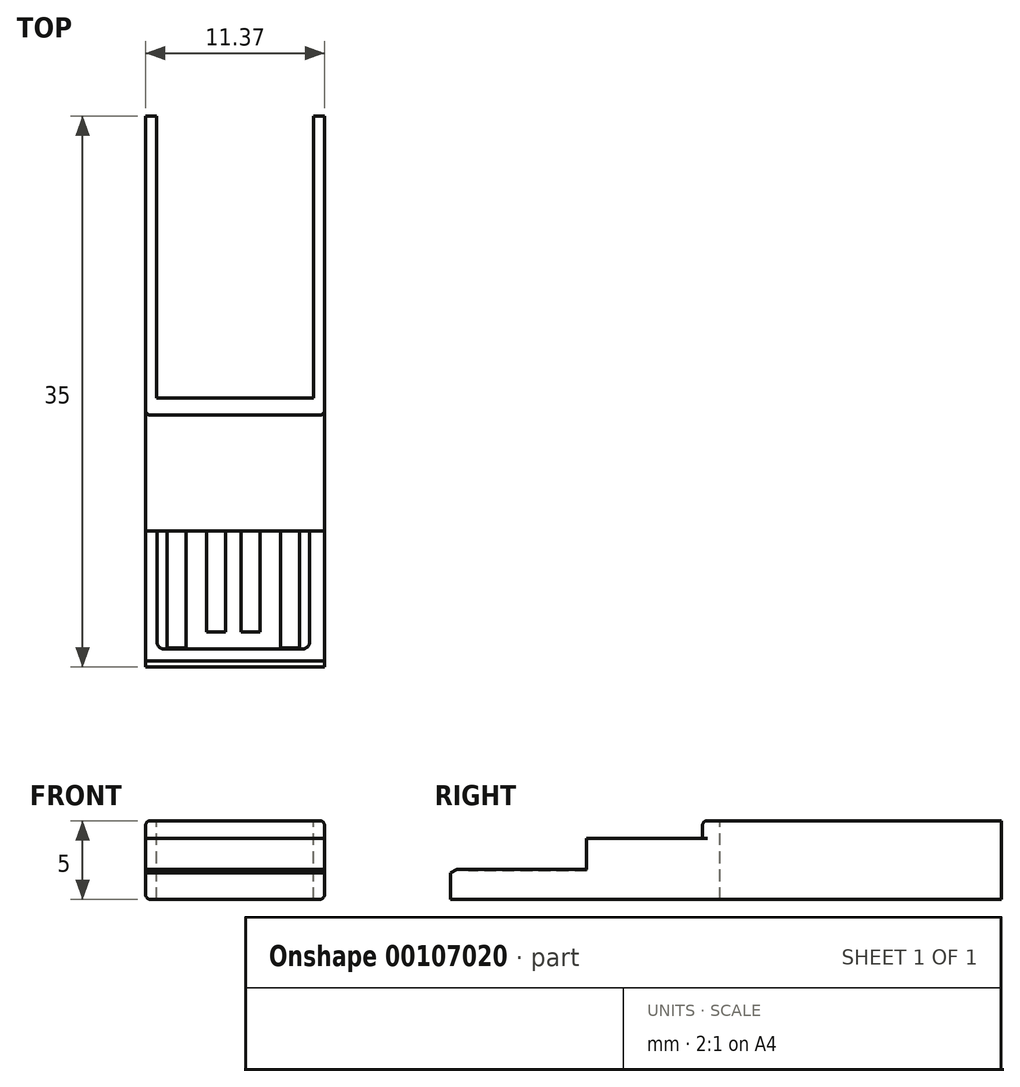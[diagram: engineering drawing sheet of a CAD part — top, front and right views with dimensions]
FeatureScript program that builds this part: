
annotation { "Feature Type Name" : "Feature", "Feature Type Description" : "" }
export const myFeature = defineFeature(function(context is Context, id is Id, definition is map)
    precondition{}
    {
        {
            var Q0;
            Q0=qCreatedBy(makeId("Front.planeOp"),FACE);
            var sketch = newSketch(context, id + "F0", { "sketchPlane" : qUnion([Q0])});
            skLineSegment(sketch, "E0.bottom", {"start": v(0, 0) * mm, "end": v(11.37, 0) * mm});
            skLineSegment(sketch, "E0.top", {"start": v(0, 1.92) * mm, "end": v(11.37, 1.92) * mm});
            skLineSegment(sketch, "E0.left", {"start": v(0, 0) * mm, "end": v(0, 1.92) * mm});
            skLineSegment(sketch, "E0.right", {"start": v(11.37, 0) * mm, "end": v(11.37, 1.92) * mm});
            skSolve(sketch);
        }
        {
            var Q0;
            Q0=qSketchRegion(id+"F0",true);
            extrude(context, id + "F1", {"entities" : qUnion([Q0]), "depth" : 35 * mm});
        }
        {
            var Q0;
            Q0=makeQuery(id+"F1.opExtrude","CAP_EDGE",EDGE,{"disambiguationData":[OSD([sQuery(id+"F0.wireOp",EDGE,"E0.top")])],"isStart":false});
            chamfer(context, id + "F2", {"entities" : qUnion([Q0]), "chamferType" : ChamferType.OFFSET_ANGLE, "width" : .4 * mm, "oppositeDirection" : false, "angle" : 30 * degree, "tangentPropagation" : true});
        }
        {
            var Q0;
            Q0=makeQuery(id+"F1.opExtrude","CAP_FACE",FACE,{"disambiguationData":[OSD([sQuery(id+"F0.wireOp",EDGE,"E0.bottom"),sQuery(id+"F0.wireOp",EDGE,"E0.top"),sQuery(id+"F0.wireOp",EDGE,"E0.left"),sQuery(id+"F0.wireOp",EDGE,"E0.right"),sQuery(id+"F0.wireOp",EDGE,"56C0QhvD-F77E-lm7p-6VUG-UG7dpPcv46jt.top"),sQuery(id+"F0.wireOp",EDGE,"56C0QhvD-F77E-lm7p-6VUG-UG7dpPcv46jt.left"),sQuery(id+"F0.wireOp",EDGE,"56C0QhvD-F77E-lm7p-6VUG-UG7dpPcv46jt.right"),sQuery(id+"F0.wireOp",EDGE,"f6b8b6c7-bbb4-4efb-80b2-3a6712df3d87.trimOffspring")])],"isStart":true});
            var sketch = newSketch(context, id + "F3", { "sketchPlane" : qUnion([Q0])});
            skLineSegment(sketch, "E1.bottom", {"start": v(0, 1.92) * mm, "end": v(-11.37, 1.92) * mm});
            skLineSegment(sketch, "E1.top", {"start": v(0, 3.87) * mm, "end": v(-11.37, 3.87) * mm});
            skLineSegment(sketch, "E1.left", {"start": v(0, 1.92) * mm, "end": v(0, 3.87) * mm});
            skLineSegment(sketch, "E1.right", {"start": v(-11.37, 1.92) * mm, "end": v(-11.37, 3.87) * mm});
            skSolve(sketch);
        }
        {
            var Q0;
            Q0=qSketchRegion(id+"F3",true);
            extrude(context, id + "F4", {"entities" : qUnion([Q0]), "operationType" : NewBodyOperationType.ADD, "oppositeDirection" : true, "depth" : 26.35 * mm});
        }
        {
            var Q0;
            {var subQ0=sQuery(id+"F0.wireOp",EDGE,"E0.top");Q0=makeQuery(id+"F5PljUPMjGb4KAi_1.boolean.opBoolean","SPLIT",FACE,{"disambiguationData":[TD([makeQuery(id+"F2.opChamfer","BLEND_FACE",FACE,{"disambiguationData":[OSD([subQ0])]})])],"derivedFrom":makeQuery(id+"F1.opExtrude","SWEPT_FACE",FACE,{"disambiguationData":[OSD([subQ0])]})});}
            var sketch = newSketch(context, id + "F5", { "sketchPlane" : qUnion([Q0])});
            skLineSegment(sketch, "E2", {"start": v(5.57, -14.35) * mm, "end": v(5.57, -24.55) * mm, "construction": true});
            skLineSegment(sketch, "E3.bottom", {"start": v(0.72, -26.36) * mm, "end": v(10.42, -26.36) * mm});
            skLineSegment(sketch, "E3.top", {"start": v(1.22, -33.86) * mm, "end": v(9.92, -33.86) * mm});
            skLineSegment(sketch, "E3.left", {"start": v(0.72, -26.36) * mm, "end": v(0.72, -33.36) * mm});
            skLineSegment(sketch, "E3.right", {"start": v(10.42, -26.36) * mm, "end": v(10.42, -33.36) * mm});
            skPoint(sketch, "E3.middle", {"position": v(5.57, -30.1) * mm});
            skPoint(sketch, "E4.visualSharp", {"position": v(0.72, -33.86) * mm});
            skArc(sketch, "E4.filletArc", {"start": v(0.72, -33.36) * mm, "mid": v(0.87, -33.7) * mm, "end": v(1.22, -33.86) * mm});
            skPoint(sketch, "E5.visualSharp", {"position": v(10.42, -33.86) * mm});
            skArc(sketch, "E5.filletArc", {"start": v(9.92, -33.86) * mm, "mid": v(10.28, -33.7) * mm, "end": v(10.42, -33.36) * mm});
            skSolve(sketch);
        }
        {
            var Q0;
            Q0=qSketchRegion(id+"F5",true);
            extrude(context, id + "F6", {"entities" : qUnion([Q0]), "operationType" : NewBodyOperationType.REMOVE, "oppositeDirection" : true, "depth" : .1 * mm});
        }
        {
            var Q0;
            Q0=makeQuery(id+"F6.boolean.opBoolean","COPY",FACE,{"derivedFrom":makeQuery(id+"F6.opExtrude","CAP_FACE",FACE,{"disambiguationData":[OSD([sQuery(id+"F5.wireOp",EDGE,"E3.bottom"),sQuery(id+"F5.wireOp",EDGE,"E3.top"),sQuery(id+"F5.wireOp",EDGE,"E3.left"),sQuery(id+"F5.wireOp",EDGE,"E3.right"),sQuery(id+"F5.wireOp",EDGE,"E4.filletArc"),sQuery(id+"F5.wireOp",EDGE,"E5.filletArc")])],"isStart":false})});
            var sketch = newSketch(context, id + "F7", { "sketchPlane" : qUnion([Q0])});
            skLineSegment(sketch, "E6.bottom", {"start": v(5.57, -26.36) * mm, "end": v(5.57, -26.36) * mm});
            skLineSegment(sketch, "E6.top", {"start": v(5.57, -33.86) * mm, "end": v(5.57, -33.86) * mm});
            skLineSegment(sketch, "E6.left", {"start": v(5.57, -26.36) * mm, "end": v(5.57, -33.86) * mm, "construction": true});
            skLineSegment(sketch, "E6.right", {"start": v(5.57, -26.36) * mm, "end": v(5.57, -33.86) * mm, "construction": true});
            skLineSegment(sketch, "E7.bottom", {"start": v(3.87, -26.36) * mm, "end": v(5.07, -26.36) * mm});
            skLineSegment(sketch, "E7.top", {"start": v(3.87, -32.77) * mm, "end": v(5.07, -32.77) * mm});
            skLineSegment(sketch, "E7.left", {"start": v(3.87, -26.36) * mm, "end": v(3.87, -32.77) * mm});
            skLineSegment(sketch, "E7.right", {"start": v(5.07, -26.36) * mm, "end": v(5.07, -32.77) * mm});
            skLineSegment(sketch, "E8.bottom", {"start": v(1.37, -26.36) * mm, "end": v(2.57, -26.36) * mm});
            skLineSegment(sketch, "E8.top", {"start": v(1.37, -33.77) * mm, "end": v(2.57, -33.77) * mm});
            skLineSegment(sketch, "E8.left", {"start": v(1.37, -26.36) * mm, "end": v(1.37, -33.77) * mm});
            skLineSegment(sketch, "E8.right", {"start": v(2.57, -26.36) * mm, "end": v(2.57, -33.77) * mm});
            skLineSegment(sketch, "E9.MirrorCS", {"start": v(7.27, -26.36) * mm, "end": v(6.07, -26.36) * mm});
            skLineSegment(sketch, "E10.MirrorCS", {"start": v(7.27, -32.77) * mm, "end": v(6.07, -32.77) * mm});
            skLineSegment(sketch, "E11.MirrorCS", {"start": v(7.27, -26.36) * mm, "end": v(7.27, -32.77) * mm});
            skLineSegment(sketch, "E12.MirrorCS", {"start": v(6.07, -26.36) * mm, "end": v(6.07, -32.77) * mm});
            skLineSegment(sketch, "E13.MirrorCS", {"start": v(9.77, -26.36) * mm, "end": v(8.57, -26.36) * mm});
            skLineSegment(sketch, "E14.MirrorCS", {"start": v(9.77, -33.77) * mm, "end": v(8.57, -33.77) * mm});
            skLineSegment(sketch, "E15.MirrorCS", {"start": v(9.77, -26.36) * mm, "end": v(9.77, -33.77) * mm});
            skLineSegment(sketch, "E16.MirrorCS", {"start": v(8.57, -26.36) * mm, "end": v(8.57, -33.77) * mm});
            skSolve(sketch);
        }
        {
            var Q0;
            Q0=qSketchRegion(id+"F7",true);
            var Q1;
            {var subQ0=sQuery(id+"F0.wireOp",EDGE,"E0.top");Q1=makeQuery(id+"F5PljUPMjGb4KAi_1.boolean.opBoolean","SPLIT",FACE,{"disambiguationData":[TD([makeQuery(id+"F2.opChamfer","BLEND_FACE",FACE,{"disambiguationData":[OSD([subQ0])]})])],"derivedFrom":makeQuery(id+"F1.opExtrude","SWEPT_FACE",FACE,{"disambiguationData":[OSD([subQ0])]})});}
            extrude(context, id + "F8", {"entities" : qUnion([Q0]), "operationType" : NewBodyOperationType.ADD, "endBound" : BoundingType.UP_TO_SURFACE, "endBoundEntityFace" : qUnion([Q1]), "depth" : 25 * mm});
        }
        {
            var Q0;
            {var subQ0=sQuery(id+"F3.wireOp",EDGE,"E1.top");Q0=makeQuery(id+"FO6QDnWpxEzhnGm_1.boolean.opBoolean","MERGE",FACE,{"derivedFrom":[makeQuery(id+"F4.opExtrude","SWEPT_FACE",FACE,{"disambiguationData":[OSD([subQ0])]}),makeQuery(id+"F5PljUPMjGb4KAi_1.opExtrude","CAP_FACE",FACE,{"disambiguationData":[OSD([subQ0])],"isStart":false}),makeQuery(id+"FO6QDnWpxEzhnGm_1.opExtrude","SWEPT_FACE",FACE,{"disambiguationData":[OSD([sQuery(id+"F6S5VhLR9gniqHa_1.wireOp",EDGE,"7c9bdd74-e41c-4fc5-a593-b1e6411b71d9.0")])]})]});}
            var sketch = newSketch(context, id + "F9", { "sketchPlane" : qUnion([Q0])});
            skLineSegment(sketch, "E17.bottom", {"start": v(11.37, 0) * mm, "end": v(0, 0) * mm});
            skLineSegment(sketch, "E17.top", {"start": v(11.37, -19) * mm, "end": v(0, -19) * mm});
            skLineSegment(sketch, "E17.left", {"start": v(11.37, 0) * mm, "end": v(11.37, -19) * mm});
            skLineSegment(sketch, "E17.right", {"start": v(0, 0) * mm, "end": v(0, -19) * mm});
            skSolve(sketch);
        }
        {
            var Q0;
            Q0 = qSketchRegion(id + "F9", true);
            extrude(context, id + "F10", {"entities" : qUnion([Q0]), "operationType" : NewBodyOperationType.ADD, "depth" : 1.13 * mm});
        }
        {
            var Q0;
            Q0=makeQuery(id+"F10.opExtrude","CAP_FACE",FACE,{"disambiguationData":[OSD([sQuery(id+"F9.wireOp",EDGE,"E17.bottom"),sQuery(id+"F9.wireOp",EDGE,"E17.top"),sQuery(id+"F9.wireOp",EDGE,"E17.left"),sQuery(id+"F9.wireOp",EDGE,"E17.right")])],"isStart":false});
            var sketch = newSketch(context, id + "F11", { "sketchPlane" : qUnion([Q0])});
            skLineSegment(sketch, "E18.bottom", {"start": v(10.68, 0) * mm, "end": v(0.68, 0) * mm});
            skLineSegment(sketch, "E18.top", {"start": v(10.69, -17.9) * mm, "end": v(0.68, -17.9) * mm});
            skLineSegment(sketch, "E18.left", {"start": v(10.68, 0) * mm, "end": v(10.69, -17.9) * mm});
            skLineSegment(sketch, "E18.right", {"start": v(0.68, 0) * mm, "end": v(0.68, -17.9) * mm});
            skSolve(sketch);
        }
        {
            var Q0;
            Q0 = qSketchRegion(id + "F11", true);
            extrude(context, id + "F12", {"entities" : qUnion([Q0]), "operationType" : NewBodyOperationType.REMOVE, "endBound" : BoundingType.THROUGH_ALL, "oppositeDirection" : true, "depth" : 25 * mm});
        }
        {
            var Q0;
            Q0=makeQuery(id+"F10.opExtrude","CAP_EDGE",EDGE,{"disambiguationData":[OSD([sQuery(id+"F9.wireOp",EDGE,"E17.top")])],"isStart":false});
            var Q1;
            Q1=makeQuery(id+"F10.opExtrude","CAP_EDGE",EDGE,{"disambiguationData":[OSD([sQuery(id+"F9.wireOp",EDGE,"E17.top")])],"isStart":true});
            fillet(context, id + "F13", {"entities" : qUnion([Q0, Q1]), "radius" : .325 * mm, "tangentPropagation" : true, "allowEdgeOverflow" : false});
        }
        {
            var Q0;
            Q0=makeQuery(id+"F10.opExtrude","CAP_EDGE",EDGE,{"disambiguationData":[OSD([sQuery(id+"F9.wireOp",EDGE,"E17.right")])],"isStart":false});
            var Q1;
            Q1=makeQuery(id+"F10.opExtrude","CAP_EDGE",EDGE,{"disambiguationData":[OSD([sQuery(id+"F9.wireOp",EDGE,"E17.left")])],"isStart":false});
            fillet(context, id + "F14", {"entities" : qUnion([Q0, Q1]), "radius" : .325 * mm, "tangentPropagation" : true, "allowEdgeOverflow" : false});
        }
        {
            var Q0;
            Q0=makeQuery(id+"F1.opExtrude","SWEPT_EDGE",EDGE,{"disambiguationData":[OSD([sQuery(id+"F0.wireOp",EDGE,"E0.bottom"),sQuery(id+"F0.wireOp",EDGE,"E0.left")])]});
            var Q1;
            Q1=makeQuery(id+"F1.opExtrude","SWEPT_EDGE",EDGE,{"disambiguationData":[OSD([sQuery(id+"F0.wireOp",EDGE,"E0.bottom"),sQuery(id+"F0.wireOp",EDGE,"E0.right")])]});
            fillet(context, id + "F15", {"entities" : qUnion([Q0, Q1]), "radius" : .325 * mm, "tangentPropagation" : true, "allowEdgeOverflow" : false});
        }
    });
